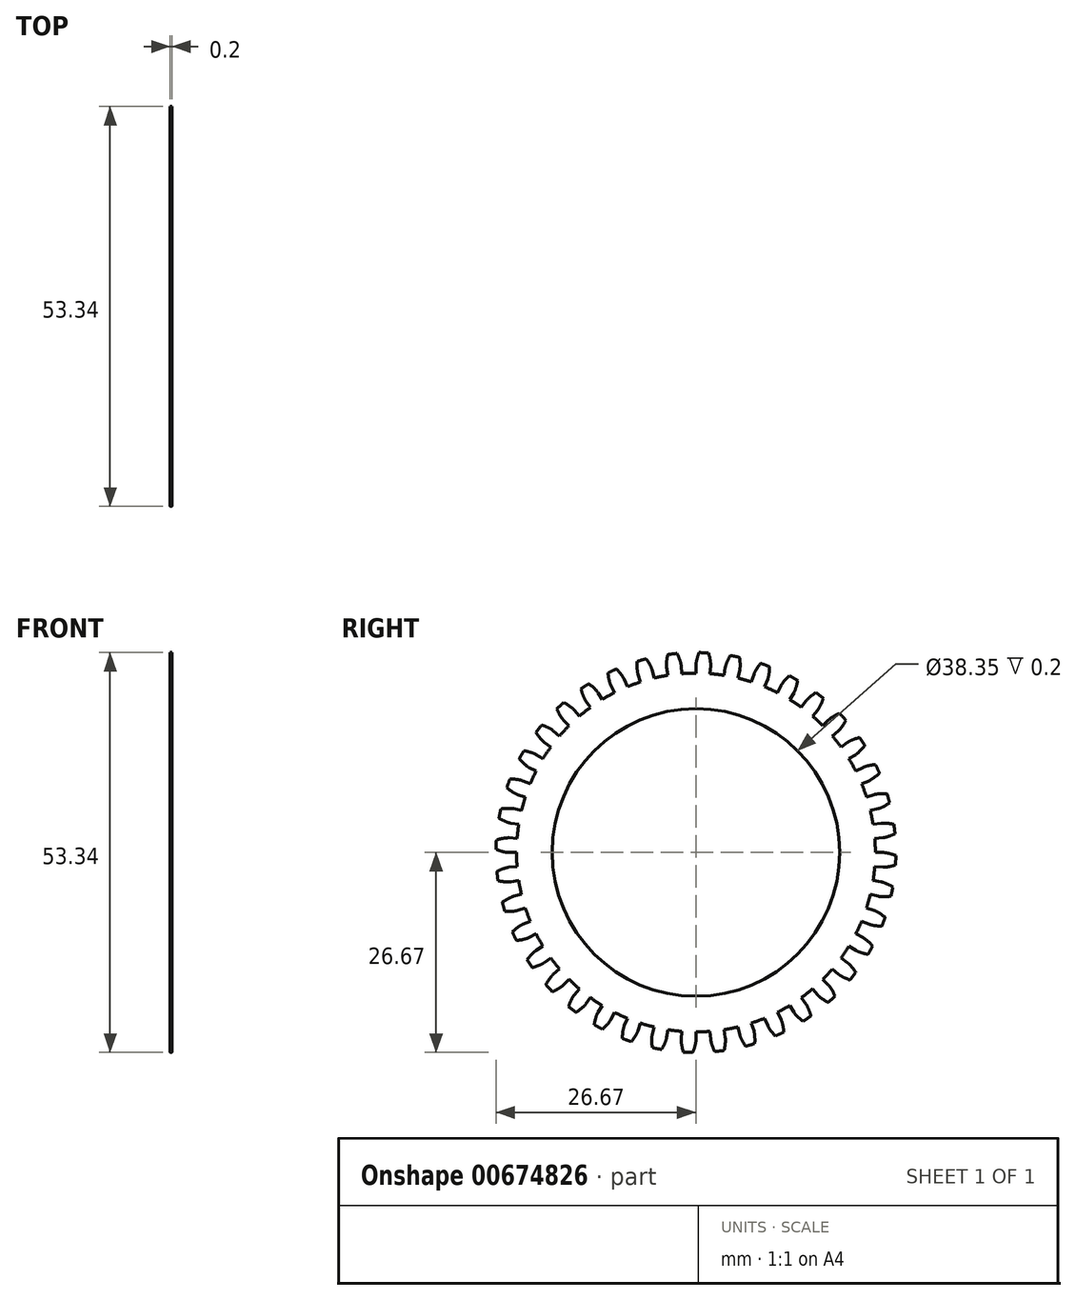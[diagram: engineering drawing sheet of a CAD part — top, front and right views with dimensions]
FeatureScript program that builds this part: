
annotation { "Feature Type Name" : "Feature", "Feature Type Description" : "" }
export const myFeature = defineFeature(function(context is Context, id is Id, definition is map)
    precondition{}
    {
        {
            assignVariable(context, id + "F0", {"name" : "NumberTeeth", "anyValue" : 40});
        }
        {
            assignVariable(context, id + "F1", {"name" : "GearThickness", "anyValue" : .2});
        }
        {
            var Q0;
            Q0=qCreatedBy(makeId("Right.planeOp"),FACE);
            var sketch = newSketch(context, id + "F2", { "sketchPlane" : qUnion([Q0])});
            skCircle(sketch, "E0", {"center": v(0, 0) * mm, "radius": 23.93 * mm});
            skCircle(sketch, "E1", {"center": v(0, 0) * mm, "radius": 25.01 * mm, "construction": true});
            skCircle(sketch, "E2", {"center": v(0, 0) * mm, "radius": 25.4 * mm, "construction": true});
            skCircle(sketch, "E3", {"center": v(0, 0) * mm, "radius": 26.67 * mm});
            skLineSegment(sketch, "E4", {"start": v(0, 0) * mm, "end": v(-25.01, 0) * mm, "construction": true});
            skLineSegment(sketch, "E5.1.0", {"start": v(0, 0) * mm, "end": v(-24.98, 1.25) * mm, "construction": true});
            skLineSegment(sketch, "E5.2.0", {"start": v(0, 0) * mm, "end": v(-24.89, 2.5) * mm, "construction": true});
            skLineSegment(sketch, "E5.3.0", {"start": v(0, 0) * mm, "end": v(-24.73, 3.74) * mm, "construction": true});
            skLineSegment(sketch, "E5.4.0", {"start": v(0, 0) * mm, "end": v(-24.52, 4.97) * mm, "construction": true});
            skLineSegment(sketch, "E5.5.0", {"start": v(0, 0) * mm, "end": v(-24.24, 6.19) * mm, "construction": true});
            skLineSegment(sketch, "E5.6.0", {"start": v(0, 0) * mm, "end": v(-23.9, 7.4) * mm, "construction": true});
            skLineSegment(sketch, "E5.7.0", {"start": v(0, 0) * mm, "end": v(-23.5, 8.58) * mm, "construction": true});
            skLineSegment(sketch, "E5.8.0", {"start": v(0, 0) * mm, "end": v(-23.04, 9.74) * mm, "construction": true});
            skLineSegment(sketch, "E5.9.0", {"start": v(0, 0) * mm, "end": v(-22.52, 10.88) * mm, "construction": true});
            skLineSegment(sketch, "E5.10.0", {"start": v(0, 0) * mm, "end": v(-21.95, 12) * mm, "construction": true});
            skLineSegment(sketch, "E5.11.0", {"start": v(0, 0) * mm, "end": v(-21.33, 13.07) * mm, "construction": true});
            skLineSegment(sketch, "E5.12.0", {"start": v(0, 0) * mm, "end": v(-20.65, 14.12) * mm, "construction": true});
            skLineSegment(sketch, "E5.13.0", {"start": v(0, 0) * mm, "end": v(-19.91, 15.14) * mm, "construction": true});
            skLineSegment(sketch, "E5.14.0", {"start": v(0, 0) * mm, "end": v(-19.13, 16.11) * mm, "construction": true});
            skLineSegment(sketch, "E5.anchor2", {"start": v(0, 0) * mm, "end": v(-19.13, 16.11) * mm, "construction": true});
            skLineSegment(sketch, "E6", {"start": v(-24.98, 1.25) * mm, "end": v(-25.05, 0) * mm, "construction": true});
            skLineSegment(sketch, "E7", {"start": v(-24.89, 2.5) * mm, "end": v(-25.14, 0) * mm, "construction": true});
            skLineSegment(sketch, "E8", {"start": v(-24.73, 3.74) * mm, "end": v(-25.3, 0.03) * mm, "construction": true});
            skLineSegment(sketch, "E9", {"start": v(-24.24, 6.19) * mm, "end": v(-25.78, 0.13) * mm, "construction": true});
            skLineSegment(sketch, "E10", {"start": v(-23.9, 7.4) * mm, "end": v(-26.11, 0.22) * mm, "construction": true});
            skLineSegment(sketch, "E11", {"start": v(-23.5, 8.58) * mm, "end": v(-26.5, 0.35) * mm, "construction": true});
            skLineSegment(sketch, "E12", {"start": v(-23.04, 9.74) * mm, "end": v(-26.94, 0.53) * mm, "construction": true});
            skLineSegment(sketch, "E13", {"start": v(-22.52, 10.88) * mm, "end": v(-27.42, 0.74) * mm, "construction": true});
            skLineSegment(sketch, "E14", {"start": v(-21.95, 12) * mm, "end": v(-27.95, 1.02) * mm, "construction": true});
            skLineSegment(sketch, "E15", {"start": v(-21.33, 13.07) * mm, "end": v(-28.52, 1.35) * mm, "construction": true});
            skLineSegment(sketch, "E16", {"start": v(-24.52, 4.97) * mm, "end": v(-25.5, 0.07) * mm, "construction": true});
            skLineSegment(sketch, "E17", {"start": v(-20.65, 14.12) * mm, "end": v(-29.12, 1.74) * mm, "construction": true});
            skLineSegment(sketch, "E18", {"start": v(-19.91, 15.14) * mm, "end": v(-29.75, 2.2) * mm, "construction": true});
            skLineSegment(sketch, "E19", {"start": v(-19.13, 16.11) * mm, "end": v(-30.41, 2.72) * mm, "construction": true});
            skLineSegment(sketch, "E20", {"start": v(0, 0) * mm, "end": v(-25, 0.98) * mm, "construction": true});
            skLineSegment(sketch, "E21", {"start": v(-23.93, 0) * mm, "end": v(-25.01, 0) * mm});
            skLineSegment(sketch, "E22.MirrorCS", {"start": v(-23.86, 1.88) * mm, "end": v(-24.94, 1.96) * mm});
            skFitSpline(sketch, "E23", {"points": [v(-25.01, 0) * mm, v(-25.05, 0) * mm, v(-25.14, 0) * mm, v(-25.3, 0.03) * mm, v(-25.5, 0.07) * mm, v(-25.78, 0.13) * mm, v(-26.11, 0.22) * mm, v(-26.5, 0.35) * mm, v(-26.94, 0.53) * mm, v(-27.42, 0.74) * mm, v(-27.95, 1.02) * mm, v(-28.52, 1.35) * mm, v(-29.12, 1.74) * mm, v(-29.75, 2.2) * mm, v(-30.41, 2.72) * mm], "startDerivative": vector(-0.75, 0) * mm, "endDerivative": vector(-1.46, 1.23) * mm});
            skLineSegment(sketch, "E24", {"start": v(-23.39, -3.2) * mm, "end": v(-30.41, 2.72) * mm, "construction": true});
            skFitSpline(sketch, "E25.MirrorCS", {"points": [v(-24.94, 1.96) * mm, v(-24.97, 1.96) * mm, v(-25.06, 1.96) * mm, v(-25.22, 1.96) * mm, v(-25.44, 1.94) * mm, v(-25.71, 1.9) * mm, v(-26.05, 1.83) * mm, v(-26.45, 1.73) * mm, v(-26.9, 1.59) * mm, v(-27.4, 1.4) * mm, v(-27.94, 1.18) * mm, v(-28.53, 0.9) * mm, v(-29.17, 0.55) * mm, v(-29.83, 0.15) * mm, v(-30.53, -0.33) * mm], "startDerivative": vector(-0.75, 0.06) * mm, "endDerivative": vector(-1.55, -1.1) * mm});
            skSolve(sketch);
        }
        {
            var Q0;
            {var subQ0=sQuery(id+"F2.wireOp",EDGE,"E0");var subQ27=makeQuery(id+"F2.imprint","INTERSECT",VERTEX,{"derivedFrom":[subQ0,sQuery(id+"F2.wireOp",EDGE,"10ea1024-8cf5-41f5-a75f-a634b86921f3.10.0")]});Q0=makeQuery(id+"F2.imprint","IMPRINT",FACE,{"disambiguationData":[TD([[makeQuery(id+"F2.imprint","IMPRINT",EDGE,{"disambiguationData":[TD([[subQ27,-1.0]])],"derivedFrom":subQ0}),1.0]])]});}
            var Q1;
            {var subQ0=sQuery(id+"F2.wireOp",EDGE,"10ea1024-8cf5-41f5-a75f-a634b86921f3.1.0");Q1=makeQuery(id+"F2.imprint","IMPRINT",FACE,{"disambiguationData":[TD([[makeQuery(id+"F2.imprint","IMPRINT",EDGE,{"derivedFrom":subQ0}),-1.0]])]});}
            var Q2;
            {var subQ7=sQuery(id+"F2.wireOp",EDGE,"10ea1024-8cf5-41f5-a75f-a634b86921f3.2.0");Q2=makeQuery(id+"F2.imprint","IMPRINT",FACE,{"disambiguationData":[TD([[makeQuery(id+"F2.imprint","IMPRINT",EDGE,{"derivedFrom":subQ7}),-1.0]])]});}
            var Q3;
            {var subQ8=sQuery(id+"F2.wireOp",EDGE,"10ea1024-8cf5-41f5-a75f-a634b86921f3.3.0");Q3=makeQuery(id+"F2.imprint","IMPRINT",FACE,{"disambiguationData":[TD([[makeQuery(id+"F2.imprint","IMPRINT",EDGE,{"derivedFrom":subQ8}),-1.0]])]});}
            var Q4;
            {var subQ2=sQuery(id+"F2.wireOp",EDGE,"10ea1024-8cf5-41f5-a75f-a634b86921f3.4.0");Q4=makeQuery(id+"F2.imprint","IMPRINT",FACE,{"disambiguationData":[TD([[makeQuery(id+"F2.imprint","IMPRINT",EDGE,{"derivedFrom":subQ2}),-1.0]])]});}
            var Q5;
            {var subQ8=sQuery(id+"F2.wireOp",EDGE,"10ea1024-8cf5-41f5-a75f-a634b86921f3.5.0");Q5=makeQuery(id+"F2.imprint","IMPRINT",FACE,{"disambiguationData":[TD([[makeQuery(id+"F2.imprint","IMPRINT",EDGE,{"derivedFrom":subQ8}),-1.0]])]});}
            var Q6;
            {var subQ3=sQuery(id+"F2.wireOp",EDGE,"10ea1024-8cf5-41f5-a75f-a634b86921f3.6.0");Q6=makeQuery(id+"F2.imprint","IMPRINT",FACE,{"disambiguationData":[TD([[makeQuery(id+"F2.imprint","IMPRINT",EDGE,{"derivedFrom":subQ3}),-1.0]])]});}
            var Q7;
            {var subQ0=sQuery(id+"F2.wireOp",EDGE,"10ea1024-8cf5-41f5-a75f-a634b86921f3.7.0");Q7=makeQuery(id+"F2.imprint","IMPRINT",FACE,{"disambiguationData":[TD([[makeQuery(id+"F2.imprint","IMPRINT",EDGE,{"derivedFrom":subQ0}),-1.0]])]});}
            var Q8;
            {var subQ5=sQuery(id+"F2.wireOp",EDGE,"10ea1024-8cf5-41f5-a75f-a634b86921f3.8.0");Q8=makeQuery(id+"F2.imprint","IMPRINT",FACE,{"disambiguationData":[TD([[makeQuery(id+"F2.imprint","IMPRINT",EDGE,{"derivedFrom":subQ5}),-1.0]])]});}
            var Q9;
            {var subQ1=sQuery(id+"F2.wireOp",EDGE,"10ea1024-8cf5-41f5-a75f-a634b86921f3.9.0");Q9=makeQuery(id+"F2.imprint","IMPRINT",FACE,{"disambiguationData":[TD([[makeQuery(id+"F2.imprint","IMPRINT",EDGE,{"derivedFrom":subQ1}),-1.0]])]});}
            var Q10;
            {var subQ5=sQuery(id+"F2.wireOp",EDGE,"10ea1024-8cf5-41f5-a75f-a634b86921f3.10.0");Q10=makeQuery(id+"F2.imprint","IMPRINT",FACE,{"disambiguationData":[TD([[makeQuery(id+"F2.imprint","IMPRINT",EDGE,{"derivedFrom":subQ5}),-1.0]])]});}
            var Q11;
            {var subQ8=sQuery(id+"F2.wireOp",EDGE,"10ea1024-8cf5-41f5-a75f-a634b86921f3.11.0");Q11=makeQuery(id+"F2.imprint","IMPRINT",FACE,{"disambiguationData":[TD([[makeQuery(id+"F2.imprint","IMPRINT",EDGE,{"derivedFrom":subQ8}),-1.0]])]});}
            var Q12;
            {var subQ2=sQuery(id+"F2.wireOp",EDGE,"10ea1024-8cf5-41f5-a75f-a634b86921f3.12.0");Q12=makeQuery(id+"F2.imprint","IMPRINT",FACE,{"disambiguationData":[TD([[makeQuery(id+"F2.imprint","IMPRINT",EDGE,{"derivedFrom":subQ2}),-1.0]])]});}
            var Q13;
            {var subQ3=sQuery(id+"F2.wireOp",EDGE,"10ea1024-8cf5-41f5-a75f-a634b86921f3.13.0");Q13=makeQuery(id+"F2.imprint","IMPRINT",FACE,{"disambiguationData":[TD([[makeQuery(id+"F2.imprint","IMPRINT",EDGE,{"derivedFrom":subQ3}),-1.0]])]});}
            var Q14;
            {var subQ0=sQuery(id+"F2.wireOp",EDGE,"10ea1024-8cf5-41f5-a75f-a634b86921f3.14.0");Q14=makeQuery(id+"F2.imprint","IMPRINT",FACE,{"disambiguationData":[TD([[makeQuery(id+"F2.imprint","IMPRINT",EDGE,{"derivedFrom":subQ0}),-1.0]])]});}
            var Q15;
            {var subQ6=sQuery(id+"F2.wireOp",EDGE,"10ea1024-8cf5-41f5-a75f-a634b86921f3.15.0");Q15=makeQuery(id+"F2.imprint","IMPRINT",FACE,{"disambiguationData":[TD([[makeQuery(id+"F2.imprint","IMPRINT",EDGE,{"derivedFrom":subQ6}),-1.0]])]});}
            var Q16;
            {var subQ5=sQuery(id+"F2.wireOp",EDGE,"10ea1024-8cf5-41f5-a75f-a634b86921f3.16.0");Q16=makeQuery(id+"F2.imprint","IMPRINT",FACE,{"disambiguationData":[TD([[makeQuery(id+"F2.imprint","IMPRINT",EDGE,{"derivedFrom":subQ5}),-1.0]])]});}
            var Q17;
            {var subQ7=sQuery(id+"F2.wireOp",EDGE,"10ea1024-8cf5-41f5-a75f-a634b86921f3.17.0");Q17=makeQuery(id+"F2.imprint","IMPRINT",FACE,{"disambiguationData":[TD([[makeQuery(id+"F2.imprint","IMPRINT",EDGE,{"derivedFrom":subQ7}),-1.0]])]});}
            var Q18;
            {var subQ5=sQuery(id+"F2.wireOp",EDGE,"10ea1024-8cf5-41f5-a75f-a634b86921f3.18.0");Q18=makeQuery(id+"F2.imprint","IMPRINT",FACE,{"disambiguationData":[TD([[makeQuery(id+"F2.imprint","IMPRINT",EDGE,{"derivedFrom":subQ5}),-1.0]])]});}
            var Q19;
            {var subQ8=sQuery(id+"F2.wireOp",EDGE,"10ea1024-8cf5-41f5-a75f-a634b86921f3.19.0");Q19=makeQuery(id+"F2.imprint","IMPRINT",FACE,{"disambiguationData":[TD([[makeQuery(id+"F2.imprint","IMPRINT",EDGE,{"derivedFrom":subQ8}),-1.0]])]});}
            var Q20;
            {var subQ8=sQuery(id+"F2.wireOp",EDGE,"E21");Q20=makeQuery(id+"F2.imprint","IMPRINT",FACE,{"disambiguationData":[TD([[makeQuery(id+"F2.imprint","IMPRINT",EDGE,{"derivedFrom":subQ8}),-1.0]])]});}
            extrude(context, id + "F3", {"entities" : qUnion([Q0, Q1, Q2, Q3, Q4, Q5, Q6, Q7, Q8, Q9, Q10, Q11, Q12, Q13, Q14, Q15, Q16, Q17, Q18, Q19, Q20]), "depth" : (getVariable(context, 'GearThickness')) * mm});
        }
        {
            var Q0;
            Q0=makeQuery(id+"F3.opExtrude","SWEPT_FACE",FACE,{"disambiguationData":[OSD([sQuery(id+"F2.wireOp",EDGE,"E25.MirrorCS")])]});
            var Q1;
            Q1=makeQuery(id+"F3.opExtrude","SWEPT_FACE",FACE,{"disambiguationData":[OSD([sQuery(id+"F2.wireOp",EDGE,"E23")])]});
            var Q2;
            Q2=makeQuery(id+"F3.opExtrude","SWEPT_FACE",FACE,{"disambiguationData":[OSD([sQuery(id+"F2.wireOp",EDGE,"E3")])]});
            var Q3;
            Q3=makeQuery(id+"F3.opExtrude","SWEPT_FACE",FACE,{"disambiguationData":[OSD([sQuery(id+"F2.wireOp",EDGE,"E22.MirrorCS")])]});
            var Q4;
            Q4=makeQuery(id+"F3.opExtrude","SWEPT_FACE",FACE,{"disambiguationData":[OSD([sQuery(id+"F2.wireOp",EDGE,"E21")])]});
            var Q5;
            Q5=makeQuery(id+"F3.opExtrude","SWEPT_FACE",FACE,{"disambiguationData":[OSD([sQuery(id+"F2.wireOp",EDGE,"E0")])]});
            circularPattern(context, id + "F4", {"faces" : qUnion([Q0, Q1, Q2, Q3, Q4]), "axis" : qUnion([Q5]), "angle" : 360 * degree, "instanceCount" : getVariable(context, 'NumberTeeth'), "equalSpace" : true, "patternType" : PatternType.FACE});
        }
        {
            var Q0;
            Q0=makeQuery(id+"F3.opExtrude","CAP_FACE",FACE,{"disambiguationData":[OSD([sQuery(id+"F2.wireOp",EDGE,"E0"),sQuery(id+"F2.wireOp",EDGE,"E3"),sQuery(id+"F2.wireOp",EDGE,"E21"),sQuery(id+"F2.wireOp",EDGE,"E22.MirrorCS"),sQuery(id+"F2.wireOp",EDGE,"E23"),sQuery(id+"F2.wireOp",EDGE,"E25.MirrorCS")])],"isStart":true});
            var sketch = newSketch(context, id + "F5", { "sketchPlane" : qUnion([Q0])});
            skCircle(sketch, "E26", {"center": v(0, 0) * mm, "radius": 19.18 * mm});
            skSolve(sketch);
        }
        {
            var Q0;
            Q0=makeQuery(id+"F5.imprint","IMPRINT",FACE,{"disambiguationData":[TD([[makeQuery(id+"F5.imprint","IMPRINT",EDGE,{"derivedFrom":sQuery(id+"F5.wireOp",EDGE,"E26")}),1.0]])]});
            extrude(context, id + "F6", {"entities" : qUnion([Q0]), "operationType" : NewBodyOperationType.REMOVE, "oppositeDirection" : true, "depth" : 7.62 * mm, "offsetDistance" : 25.4 * mm});
        }
    });
